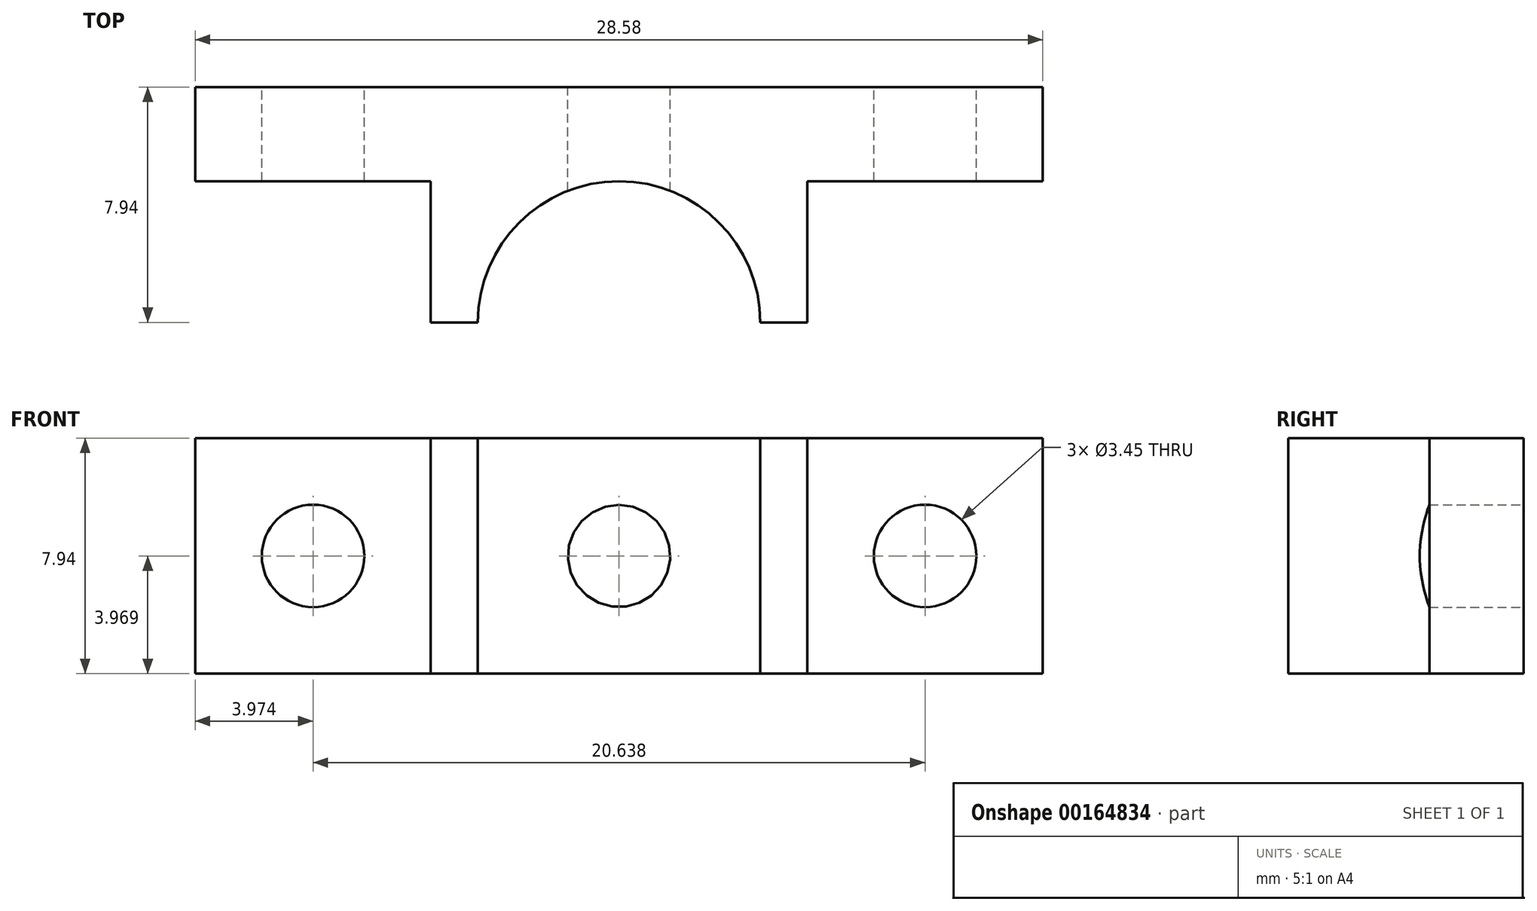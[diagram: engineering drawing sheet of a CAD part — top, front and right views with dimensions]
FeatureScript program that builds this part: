
annotation { "Feature Type Name" : "Feature", "Feature Type Description" : "" }
export const myFeature = defineFeature(function(context is Context, id is Id, definition is map)
    precondition{}
    {
        {
            var Q0;
            Q0=qCreatedBy(makeId("Top.planeOp"),FACE);
            var sketch = newSketch(context, id + "F0", { "sketchPlane" : qUnion([Q0])});
            skLineSegment(sketch, "E0", {"start": v(0, 0) * mm, "end": v(9.53, 0) * mm, "construction": true});
            skArc(sketch, "E1", {"start": v(9.53, 0) * mm, "mid": v(4.76, 4.76) * mm, "end": v(0, 0) * mm});
            skLineSegment(sketch, "E2", {"start": v(0, 0) * mm, "end": v(-1.59, 0) * mm});
            skLineSegment(sketch, "E3", {"start": v(-1.59, 0) * mm, "end": v(-1.59, 4.76) * mm});
            skLineSegment(sketch, "E4", {"start": v(-1.59, 4.76) * mm, "end": v(-9.53, 4.76) * mm});
            skLineSegment(sketch, "E5", {"start": v(-9.53, 4.76) * mm, "end": v(-9.53, 7.94) * mm});
            skLineSegment(sketch, "E6", {"start": v(-9.53, 7.94) * mm, "end": v(19.05, 7.94) * mm});
            skLineSegment(sketch, "E7", {"start": v(19.05, 7.94) * mm, "end": v(19.05, 4.76) * mm});
            skLineSegment(sketch, "E8", {"start": v(19.05, 4.76) * mm, "end": v(11.11, 4.76) * mm});
            skLineSegment(sketch, "E9", {"start": v(11.11, 4.76) * mm, "end": v(11.11, 0) * mm});
            skLineSegment(sketch, "E10", {"start": v(11.11, 0) * mm, "end": v(9.53, 0) * mm});
            skSolve(sketch);
        }
        {
            var Q0;
            Q0 = qSketchRegion(id + "F0", true);
            extrude(context, id + "F1", {"entities" : qUnion([Q0]), "depth" : 7.94 * mm});
        }
        {
            var Q0;
            Q0=makeQuery(id+"F1.opExtrude","SWEPT_FACE",FACE,{"disambiguationData":[OSD([sQuery(id+"F0.wireOp",EDGE,"E6")])]});
            var sketch = newSketch(context, id + "F2", { "sketchPlane" : qUnion([Q0])});
            skLineSegment(sketch, "E11.bottom", {"start": v(9.53, 3.97) * mm, "end": v(5.56, 3.97) * mm, "construction": true});
            skLineSegment(sketch, "E11.top", {"start": v(9.53, 7.94) * mm, "end": v(5.56, 7.94) * mm, "construction": true});
            skLineSegment(sketch, "E11.left", {"start": v(9.53, 3.97) * mm, "end": v(9.53, 7.94) * mm, "construction": true});
            skLineSegment(sketch, "E11.right", {"start": v(5.56, 3.97) * mm, "end": v(5.56, 7.94) * mm, "construction": true});
            skLineSegment(sketch, "E12.bottom", {"start": v(-19.05, 3.97) * mm, "end": v(-15.08, 3.97) * mm, "construction": true});
            skLineSegment(sketch, "E12.top", {"start": v(-19.05, 7.94) * mm, "end": v(-15.08, 7.94) * mm, "construction": true});
            skLineSegment(sketch, "E12.left", {"start": v(-19.05, 3.97) * mm, "end": v(-19.05, 7.94) * mm, "construction": true});
            skLineSegment(sketch, "E12.right", {"start": v(-15.08, 3.97) * mm, "end": v(-15.08, 7.94) * mm, "construction": true});
            skLineSegment(sketch, "E13", {"start": v(-4.76, 0) * mm, "end": v(-4.76, 7.94) * mm, "construction": true});
            skCircle(sketch, "E14", {"center": v(5.56, 3.97) * mm, "radius": 1.73 * mm});
            skCircle(sketch, "E15", {"center": v(-15.08, 3.97) * mm, "radius": 1.73 * mm});
            skCircle(sketch, "E16", {"center": v(-4.76, 3.97) * mm, "radius": 1.73 * mm});
            skSolve(sketch);
        }
        {
            var Q0;
            Q0 = qSketchRegion(id + "F2", true);
            var Q1;
            Q1=makeQuery(id+"F1.opExtrude","SWEPT_FACE",FACE,{"disambiguationData":[OSD([sQuery(id+"F0.wireOp",EDGE,"E2")])]});
            extrude(context, id + "F3", {"entities" : qUnion([Q0]), "operationType" : NewBodyOperationType.REMOVE, "endBound" : BoundingType.UP_TO_SURFACE, "oppositeDirection" : true, "endBoundEntityFace" : qUnion([Q1]), "depth" : 25.4 * mm});
        }
    });
